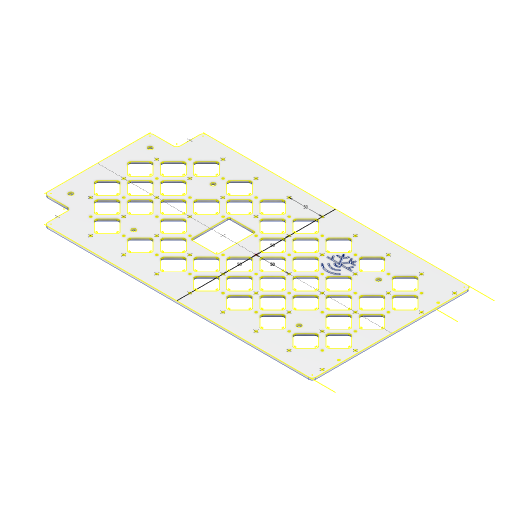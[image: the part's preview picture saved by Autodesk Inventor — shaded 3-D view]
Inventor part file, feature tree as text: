
AUTODESK INVENTOR PART (.ipt)
format: ipt  version: 2023 (Build 270158000, 158)  size: 1,654,784 bytes
history: native  units: mm
features: sketch x10, extrude x9, other x6, fillet x4, projected_geometry x1
ambient origin geometry x8: Origin, YZ Plane, XZ Plane, XY Plane, X Axis, Y Axis, Z Axis, Center Point
bodies: Solid1 (feature_tree)
feature tree (30):
  other  "Blocks"
  extrude  "Extrusion1"  Depth=240.0mm
  sketch  "Sketch2"  dims[d2=40.0mm d3=40.0mm d4=35.0mm]
  sketch  "Sketch3"  dims[d5=130.0mm d7=240.0mm]
  sketch  "Sketch4"  dims[d8=6.6mm d9=6.6mm]
  extrude  "OctagonE"  Depth=40.0mm
  fillet  "Fillet4"  Radius=35.0mm
  extrude  "Mount Hole"  Depth=240.0mm
  extrude  "Mount Hole NE"  Depth=6.6mm
  extrude  "OctagonN"  Depth=120.0mm
  fillet  "Fillet5"  Radius=120.0mm
  other  "Mount Hole Pattern"
  other  "Octagon E Pattern"
  other  "Octagon N Pattern"
  sketch  "Sketch Driven Pattern4"  dims[d11=6.6mm d12=120.0mm d13=120.0mm]
  extrude  "logo extrusion"  Depth=125.0mm
  extrude  "Extrusion8"  TaperAngle=0.0deg  [1 undecoded]
  fillet  "Fillet2"  Radius=20.0mm
  extrude  "Remove top tabs"  Depth=5.0mm
  extrude  "Extrusion10"  Depth=5.0mm
  fillet  "Fillet3"  Radius=5.0mm
  sketch  "Sketch10"  dims[d39=67.983078mm d40=50.0mm d41=14.644661mm d42=4.0mm d43=4.0mm d44=4.0mm d45=4.0mm d46=3.3mm d49=50.0mm d51=50.0mm d52=30.0mm d54=50.0mm d57=30.0mm d59=50.0mm d60=50.0mm d62=50.0mm d72=4.0mm d73=4.0mm d74=4.0mm d75=4.0mm d76=0.0mm d77=0.0mm d78=0.0mm d79=0.0mm d80=0.0mm d81=0.0mm d82=50.0mm d84=50.0mm d85=10.0mm d87=10.0mm d89=3.3mm d90=25.0mm d91=25.0mm d92=0.0mm d93=0.0mm d94=10.0mm d95=0.0mm d97=40.0mm d98=50.0mm d99=5.0mm d100=3.0mm d102=0.0mm d103=0.0mm d104=2.0mm d105=0.0mm d106=0.0mm d107=80.0mm d109=25.0mm d110=10.0mm d112=10.0mm d114=0.0mm d115=0.0mm d116=5.0mm d118=2.0mm d119=3.0mm d120=2.0mm]
  sketch  "Sketch1"  dims[d0=480.0mm d1=240.0mm]
  sketch  "Sketch5"  dims[d14=250.0mm d15=125.0mm]
  other  "logo"
  sketch  "Sketch7"  dims[d20=3.175mm d21=0.0mm d22=0.0mm d24=20.0mm]
  sketch  "Sketch8"  dims[d25=3.3mm d30=5.0mm]
  sketch  "Sketch9"  dims[d31=5.0mm d32=5.0mm d34=5.0mm]
  projected_geometry  "Projected Loop2"
  other  "logo:1"
note: 1 required parameter value undecoded (feature->parameter linkage not recoverable at this tier; creation-order binding heuristic only, values carry confidence <= 0.55)
